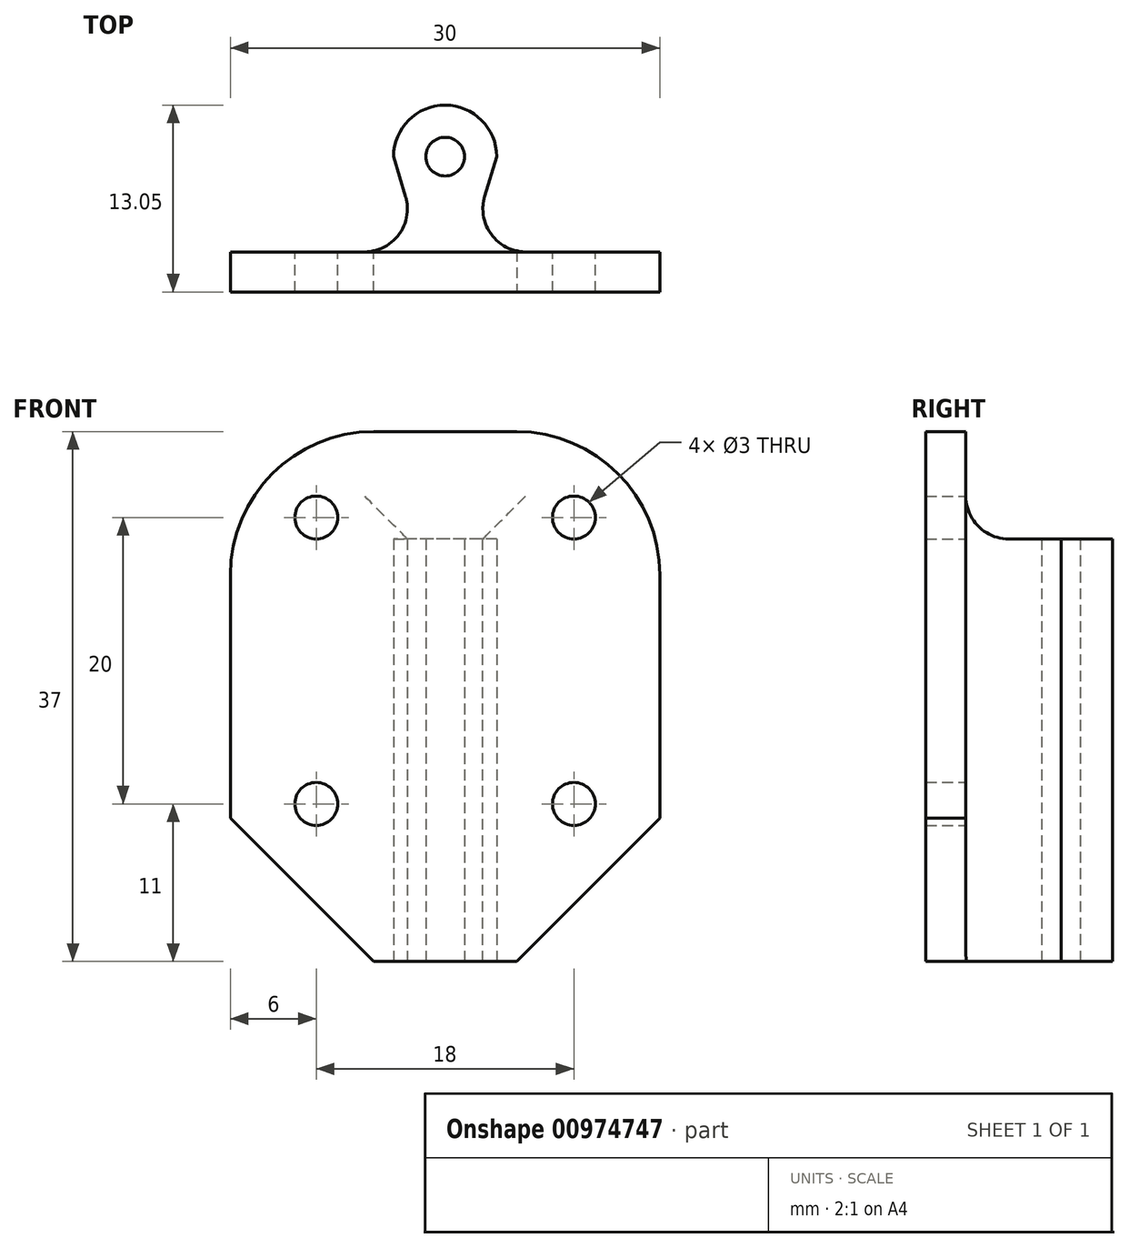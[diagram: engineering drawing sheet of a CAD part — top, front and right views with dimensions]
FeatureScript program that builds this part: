
annotation { "Feature Type Name" : "Feature", "Feature Type Description" : "" }
export const myFeature = defineFeature(function(context is Context, id is Id, definition is map)
    precondition{}
    {
        {
            var Q0;
            Q0=qCreatedBy(makeId("Top.planeOp"),FACE);
            var sketch = newSketch(context, id + "F0", { "sketchPlane" : qUnion([Q0])});
            skLineSegment(sketch, "E0", {"start": v(15, 0) * mm, "end": v(-15, 0) * mm});
            skLineSegment(sketch, "E1", {"start": v(-15, 0) * mm, "end": v(-15, 2.8) * mm});
            skLineSegment(sketch, "E2", {"start": v(-15, 2.8) * mm, "end": v(15, 2.8) * mm});
            skLineSegment(sketch, "E3", {"start": v(15, 2.8) * mm, "end": v(15, 0) * mm});
            skCircle(sketch, "E4", {"center": v(0, 9.45) * mm, "radius": 1.35 * mm});
            skCircle(sketch, "E5", {"center": v(0, 9.45) * mm, "radius": 3.6 * mm});
            skLineSegment(sketch, "E6", {"start": v(-3.6, 9.45) * mm, "end": v(-1.6, 2.8) * mm});
            skLineSegment(sketch, "E7", {"start": v(3.6, 9.45) * mm, "end": v(1.6, 2.8) * mm});
            skSolve(sketch);
        }
        {
            var Q0;
            {var subQ0=sQuery(id+"F0.wireOp",EDGE,"E6");var subQ1=sQuery(id+"F0.wireOp",EDGE,"E2");var subQ2=makeQuery(id+"F0.imprint","INTERSECT",VERTEX,{"derivedFrom":[subQ1,subQ0]});Q0=makeQuery(id+"F0.imprint","IMPRINT",FACE,{"disambiguationData":[TD([[makeQuery(id+"F0.imprint","IMPRINT",EDGE,{"disambiguationData":[TD([[subQ2,-1.0]])],"derivedFrom":subQ1}),1.0]])]});}
            var Q1;
            Q1=makeQuery(id+"F0.imprint","IMPRINT",FACE,{"disambiguationData":[TD([[makeQuery(id+"F0.imprint","IMPRINT",EDGE,{"derivedFrom":sQuery(id+"F0.wireOp",EDGE,"E4")}),-1.0]])]});
            var Q2;
            Q2=makeQuery(id+"F0.imprint","IMPRINT",FACE,{"disambiguationData":[TD([[makeQuery(id+"F0.imprint","IMPRINT",EDGE,{"derivedFrom":sQuery(id+"F0.wireOp",EDGE,"E0")}),-1.0]])]});
            var Q3;
            {var subQ0=sQuery(id+"F0.wireOp",EDGE,"E6");var subQ1=sQuery(id+"F0.wireOp",EDGE,"E5");var subQ2=makeQuery(id+"F0.imprint","INTERSECT",VERTEX,{"disambiguationData":[OD(0.0)],"derivedFrom":[subQ1,subQ0]});Q3=makeQuery(id+"F0.imprint","IMPRINT",FACE,{"disambiguationData":[TD([[makeQuery(id+"F0.imprint","IMPRINT",EDGE,{"disambiguationData":[TD([[subQ2,-1.0]])],"derivedFrom":subQ1}),1.0]])]});}
            var Q4;
            {var subQ0=sQuery(id+"F0.wireOp",EDGE,"E7");var subQ1=sQuery(id+"F0.wireOp",EDGE,"E5");var subQ2=makeQuery(id+"F0.imprint","INTERSECT",VERTEX,{"disambiguationData":[OD(0.0)],"derivedFrom":[subQ1,subQ0]});Q4=makeQuery(id+"F0.imprint","IMPRINT",FACE,{"disambiguationData":[TD([[makeQuery(id+"F0.imprint","IMPRINT",EDGE,{"disambiguationData":[TD([[subQ2,1.0]])],"derivedFrom":subQ1}),1.0]])]});}
            extrude(context, id + "F1", {"entities" : qUnion([Q0, Q1, Q2, Q3, Q4]), "depth" : 29.5 * mm, "offsetDistance" : 25 * mm});
        }
        {
            var Q0;
            Q0=makeQuery(id+"F0.imprint","IMPRINT",FACE,{"disambiguationData":[TD([[makeQuery(id+"F0.imprint","IMPRINT",EDGE,{"derivedFrom":sQuery(id+"F0.wireOp",EDGE,"E0")}),-1.0]])]});
            extrude(context, id + "F2", {"entities" : qUnion([Q0]), "operationType" : NewBodyOperationType.ADD, "depth" : 37 * mm, "offsetDistance" : 25 * mm});
        }
        {
            var Q0;
            Q0=makeQuery(id+"F1.opExtrude","SWEPT_EDGE",EDGE,{"disambiguationData":[OSD([sQuery(id+"F0.wireOp",EDGE,"E2"),sQuery(id+"F0.wireOp",EDGE,"E6")])]});
            var Q1;
            Q1=makeQuery(id+"F1.opExtrude","SWEPT_EDGE",EDGE,{"disambiguationData":[OSD([sQuery(id+"F0.wireOp",EDGE,"E2"),sQuery(id+"F0.wireOp",EDGE,"E7")])]});
            var Q2;
            {var subQ0=sQuery(id+"F0.wireOp",EDGE,"E2");Q2=makeQuery(id+"F2.boolean.opBoolean","INTERSECT",EDGE,{"derivedFrom":[makeQuery(id+"F1.opExtrude","CAP_FACE",FACE,{"disambiguationData":[OSD([sQuery(id+"F0.wireOp",EDGE,"E0"),sQuery(id+"F0.wireOp",EDGE,"E1"),subQ0,sQuery(id+"F0.wireOp",EDGE,"E3"),sQuery(id+"F0.wireOp",EDGE,"E4"),sQuery(id+"F0.wireOp",EDGE,"E5"),sQuery(id+"F0.wireOp",EDGE,"E6"),sQuery(id+"F0.wireOp",EDGE,"E7")])],"isStart":false}),makeQuery(id+"F2.opExtrude","SWEPT_FACE",FACE,{"disambiguationData":[OSD([subQ0])]})]});}
            fillet(context, id + "F3", {"entities" : qUnion([Q0, Q1, Q2]), "radius" : 3 * mm, "tangentPropagation" : true, "allowEdgeOverflow" : false});
        }
        {
            var Q0;
            Q0=makeQuery(id+"F2.opExtrude","CAP_EDGE",EDGE,{"disambiguationData":[OSD([sQuery(id+"F0.wireOp",EDGE,"E1")])],"isStart":false});
            var Q1;
            Q1=makeQuery(id+"F2.opExtrude","CAP_EDGE",EDGE,{"disambiguationData":[OSD([sQuery(id+"F0.wireOp",EDGE,"E3")])],"isStart":false});
            fillet(context, id + "F4", {"entities" : qUnion([Q0, Q1]), "radius" : 10 * mm, "tangentPropagation" : true, "allowEdgeOverflow" : false});
        }
        {
            var Q0;
            Q0=makeQuery(id+"F1.opExtrude","CAP_EDGE",EDGE,{"disambiguationData":[OSD([sQuery(id+"F0.wireOp",EDGE,"E3")])],"isStart":true});
            var Q1;
            Q1=makeQuery(id+"F1.opExtrude","CAP_EDGE",EDGE,{"disambiguationData":[OSD([sQuery(id+"F0.wireOp",EDGE,"E1")])],"isStart":true});
            chamfer(context, id + "F5", {"entities" : qUnion([Q0, Q1]), "width" : 10 * mm, "tangentPropagation" : true});
        }
        {
            var Q0;
            {var subQ0=sQuery(id+"F0.wireOp",EDGE,"E2");Q0=makeQuery(id+"F2.boolean.opBoolean","MERGE",FACE,{"derivedFrom":[makeQuery(id+"F1.opExtrude","SWEPT_FACE",FACE,{"disambiguationData":[OSD([subQ0]),TDD([makeQuery(id+"F0.imprint","IMPRINT",EDGE,{"disambiguationData":[TD([[makeQuery(id+"F0.imprint","INTERSECT",VERTEX,{"derivedFrom":[sQuery(id+"F0.wireOp",EDGE,"E1"),subQ0]}),-1.0]])],"derivedFrom":subQ0})])]}),makeQuery(id+"F1.opExtrude","SWEPT_FACE",FACE,{"disambiguationData":[OSD([subQ0]),TDD([makeQuery(id+"F0.imprint","IMPRINT",EDGE,{"disambiguationData":[TD([[makeQuery(id+"F0.imprint","INTERSECT",VERTEX,{"derivedFrom":[subQ0,sQuery(id+"F0.wireOp",EDGE,"E3")]}),1.0]])],"derivedFrom":subQ0})])]}),makeQuery(id+"F2.opExtrude","SWEPT_FACE",FACE,{"disambiguationData":[OSD([subQ0])]})]});}
            var sketch = newSketch(context, id + "F6", { "sketchPlane" : qUnion([Q0])});
            skCircle(sketch, "E8", {"center": v(-9, 31) * mm, "radius": 1.5 * mm});
            skCircle(sketch, "E9", {"center": v(9, 31) * mm, "radius": 1.5 * mm});
            skCircle(sketch, "E10", {"center": v(-9, 11) * mm, "radius": 1.5 * mm});
            skCircle(sketch, "E11", {"center": v(9, 11) * mm, "radius": 1.5 * mm});
            skSolve(sketch);
        }
        {
            var Q0;
            Q0 = qSketchRegion(id + "F6", true);
            extrude(context, id + "F7", {"entities" : qUnion([Q0]), "operationType" : NewBodyOperationType.REMOVE, "oppositeDirection" : true, "depth" : 25 * mm, "offsetDistance" : 25 * mm});
        }
    });
